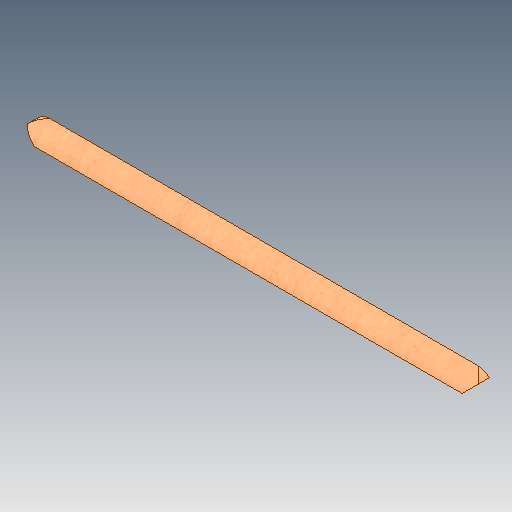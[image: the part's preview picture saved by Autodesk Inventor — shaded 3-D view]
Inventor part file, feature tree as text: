
AUTODESK INVENTOR PART (.ipt)
format: ipt  version: 2018.2 (Build 222227000, 227)  size: 140,800 bytes
history: native  units: mm
features: extrude x3, sketch x3, fillet x1, chamfer x1, mirror x1, projected_geometry x1
ambient origin geometry x8: Origin, YZ Plane, XZ Plane, XY Plane, X Axis, Y Axis, Z Axis, Center Point
bodies: Solid1 (feature_tree)
feature tree (10):
  extrude  "Extrusion1"  Depth=12.7mm
  fillet  "Fillet1"  Radius=365.4mm
  chamfer  "Chamfer1"  Distance=2.0mm Angle=45.0deg
  extrude  "Extrusion2"  Depth=12.699987mm
  mirror  "Mirror1"
  extrude  "Extrusion3"  TaperAngle=45.0deg  [1 undecoded]
  sketch  "Sketch1"  dims[d0=12.7mm d1=12.7mm d2=365.4mm]
  sketch  "Sketch2"  dims[d3=0.0mm]
  sketch  "Sketch3"  dims[d4=6.35mm d5=2.0mm d6=45.0deg d7=12.699987mm d11=45.0deg d12=10.0mm d13=0.0mm d14=3.175mm d15=6.35mm d16=0.0mm d17=0.0mm]
  projected_geometry  "Projected Loop1"
note: 1 required parameter value undecoded (feature->parameter linkage not recoverable at this tier; creation-order binding heuristic only, values carry confidence <= 0.55)
